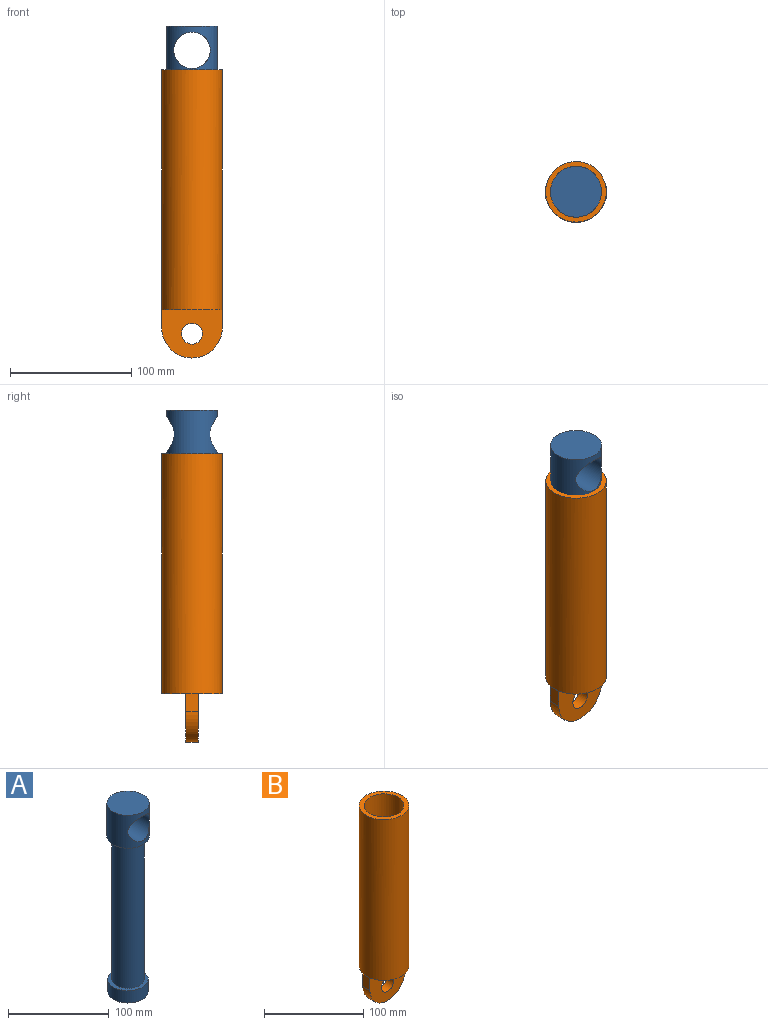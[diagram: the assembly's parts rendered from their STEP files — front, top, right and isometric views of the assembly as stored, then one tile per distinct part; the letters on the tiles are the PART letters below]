
ASSEMBLY  parts=2 mates=1
PART A: 9 faces, bbox 42x42x229 mm
  f0: plane 40x40mm, normal (0,0,-1), area 1256.6mm2, adj f1
  f1: cylinder r=20mm len=40mm, axis (0,0,-1), area 1885mm2, adj f0,f2
  f2: plane 40x40mm, normal (0,0,1), area 452.4mm2, adj f1,f3
  f3: cylinder r=16mm len=171mm, axis (0,0,-1), area 17190.8mm2, adj f2,f8
  f4: cylinder r=21mm len=42mm, axis (0,0,-1), area 3747.9mm2, adj f5,f6,f7
  f5: plane 42x42mm, normal (0,0,1), area 1385.4mm2, adj f4
  f6: plane 42x42mm, normal (0,0,-1), area 251.3mm2, adj f4,f8
  f7: cylinder r=15mm len=42mm, axis (0,-1,0), area 3390.8mm2, adj f4
  f8: cone r=16mm half-angle=45deg, axis (0,0,1), area 466.5mm2, adj f3,f6
PART B: 16 faces, bbox 50x50x238 mm
  f0: plane 48.99x20mm, normal (0,0,-1), area 733.4mm2, adj f5,f14
  f1: plane 50x50mm, normal (0,0,1), area 706.9mm2, adj f2,f5
  f2: cylinder r=20mm len=193mm, axis (0,0,-1), area 24253.1mm2, adj f1,f3
  f3: plane 40x40mm, normal (0,0,1), area 1256.6mm2, adj f2
  f4: plane 48.99x20mm, normal (0,0,-1), area 733.4mm2, adj f5,f15
  f5: cylinder r=25mm len=198mm, axis (0,0,-1), area 31101.8mm2, adj f0,f1,f4,f6,f7,f8,f11
  f6: plane 5x0.51mm, normal (0,0,1), area 0.8mm2, adj f5,f10,f15
  f7: plane 5x0.51mm, normal (0,0,1), area 0.8mm2, adj f5,f10,f14
  f8: plane 5x0.51mm, normal (0,0,1), area 0.8mm2, adj f5,f13,f15
  f9: cylinder r=25mm len=50mm, axis (0,1,0), area 785.4mm2, adj f10,f13,f14,f15
  f10: plane 15x10mm, normal (1,0,0), area 150mm2, adj f6,f7,f9,f14,f15
  f11: plane 5x0.51mm, normal (0,0,1), area 0.8mm2, adj f5,f13,f14
  f12: cylinder r=8.6mm len=17.2mm, axis (0,1,0), area 540.4mm2, adj f14,f15
  f13: plane 15x10mm, normal (-1,0,0), area 150mm2, adj f8,f9,f11,f14,f15
  f14: plane 50x40mm, normal (0,-1,0), area 1499.4mm2, adj f0,f7,f9,f10,f11,f12,f13
  f15: plane 50x40mm, normal (0,1,0), area 1499.4mm2, adj f4,f6,f8,f9,f10,f12,f13
PLACE A t=(-59.7,69.78,70.54)mm
PLACE B t=(-59.7,69.78,65.54)mm fixed
MATE slider A.f1 <-> B.f2  axis (0,0,-1) through (-59.7,69.78,70.54)mm
